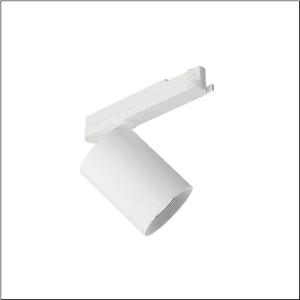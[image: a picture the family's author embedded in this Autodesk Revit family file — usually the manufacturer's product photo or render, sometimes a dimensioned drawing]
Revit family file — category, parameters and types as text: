
# Revit family: spot_21_51se14mbd5b
name_source: partatom
category: Lighting Fixtures
units: mm (PartAtom-declared; Revit-internal decimal feet)

## family parameters
Cut with Voids When Loaded = No
Host = Face
Light Source = No
Part Type = Normal
Room Calculation Point = No
Round Connector Dimension = Use Diameter
Shared = No

## types (1)
- --- (1 x LED, 5490 lm, 41.5 W, 4000K)
    Apparent Load = 42 VA
    CIE Flux Codes = 96 99 100 100 100
    Color Rendering = 90
    Color Temperature = 4000K
    Default Elevation = 1800 mm
    Description = Spot 21, directional spotlight, light control with lens, of PMMA, LED rated luminous flux: 5.270lm, light colour: 940, control gear: ECG Multilumen, with 3-phase adapter, mains connection: 220..240V, AC, 50/60Hz, of aluminium, traffic white (RAL 9016), length: 213mm, diameter: 105mm, protection rating (complete): IP20, insulation class (complete): insulation class I (protective earthing), certification: CE, impact resistance: IK02, permissible ambient temperature for indoor applications: -20..+40°C, packaging unit: 1 piece
    Height = 175 mm
    Lamp = 1 x LED
    Lamp Light Flux = 5490 lm
    Lamp Power = 41.5 W
    Lamp count = 1
    Length = 105 mm
    Luminous efficacy = 132 lm/W
    Manufacturer = Siteco
    ModVariant = No
    Model = 51SE14MBD5B
    Mounting Place = Ceiling
    Mounting Type = Pendant
    Number of Poles = 1
    OnlyDefault = Yes
    Power Factor = 1
    Product Name = Spot 21
    Product group = directional spotlight
    ProductGroupID = 905
    Protection Class = Protection class I
    Protection Degree = IP 20
    RLX_Detail_Level = 1
    RLX_Emergency_Light_Flux = 0 lm
    RLX_Emergency_Type = 0
    RLX_Emergency_Type_DB = No
    RlxData = <blob elided: 17629 chars, md5=7b822a5b>
    Socket = socket
    Standby Power = 0 W
    System Light Flux = 5490 lm
    System Power = 42 W
    Type Comments = factory setting: luminous flux: 100 % | (ON | ON | ON | ON) | 1050 mA
    Type Image = l_1003976.jpg
    URL = http://relux.com
    VarID = @adj_093105
    Voltage = 0 V
    Weight = 0.00 kg
    Width = 0 mm  [stored 0 ft]

note: [stored X ft] marks values corroborated as IEEE doubles in the binary element streams (Revit-internal decimal feet)

## geometry (parser evidence)
native form markers: Blend x4, Sweep x10
no freeform markers — native parametric forms only
